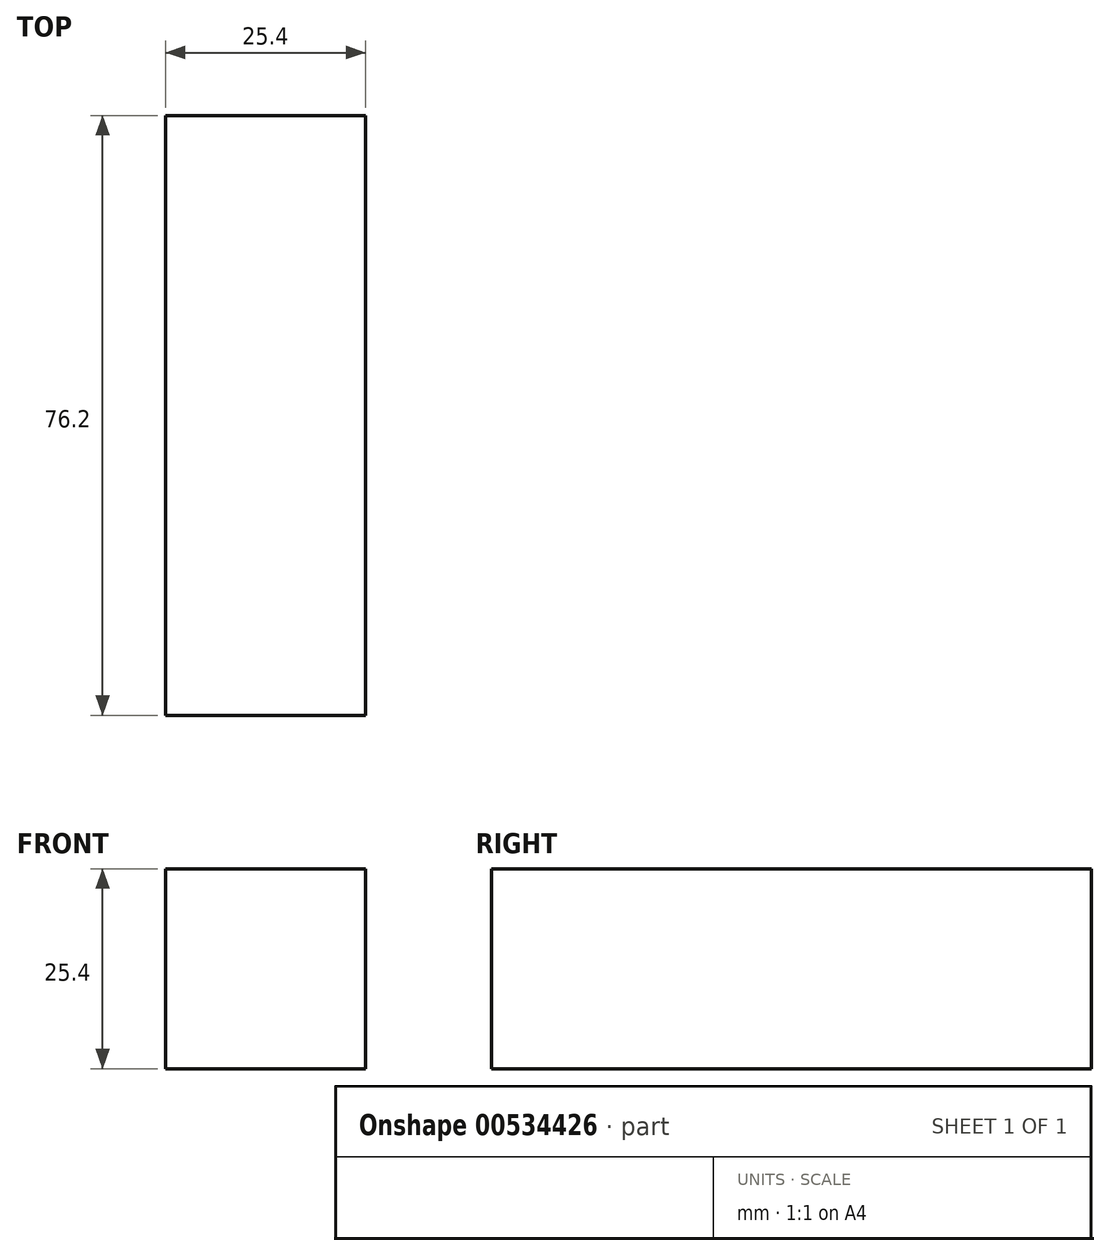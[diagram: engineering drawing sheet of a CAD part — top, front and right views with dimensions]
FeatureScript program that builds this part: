
annotation { "Feature Type Name" : "Feature", "Feature Type Description" : "" }
export const myFeature = defineFeature(function(context is Context, id is Id, definition is map)
    precondition{}
    {
        {
            var Q0;
            Q0=qCreatedBy(makeId("Front.planeOp"),FACE);
            var sketch = newSketch(context, id + "F0", { "sketchPlane" : qUnion([Q0])});
            skLineSegment(sketch, "E0.bottom", {"start": v(-46.14, 30.73) * mm, "end": v(-20.74, 30.73) * mm});
            skLineSegment(sketch, "E0.top", {"start": v(-46.14, 5.33) * mm, "end": v(-20.74, 5.33) * mm});
            skLineSegment(sketch, "E0.left", {"start": v(-46.14, 30.73) * mm, "end": v(-46.14, 5.33) * mm});
            skLineSegment(sketch, "E0.right", {"start": v(-20.74, 30.73) * mm, "end": v(-20.74, 5.33) * mm});
            skSolve(sketch);
        }
        {
            var Q0;
            Q0 = qSketchRegion(id + "F0", true);
            extrude(context, id + "F1", {"entities" : qUnion([Q0]), "depth" : 76.2 * mm, "offsetDistance" : 25.4 * mm});
        }
    });
